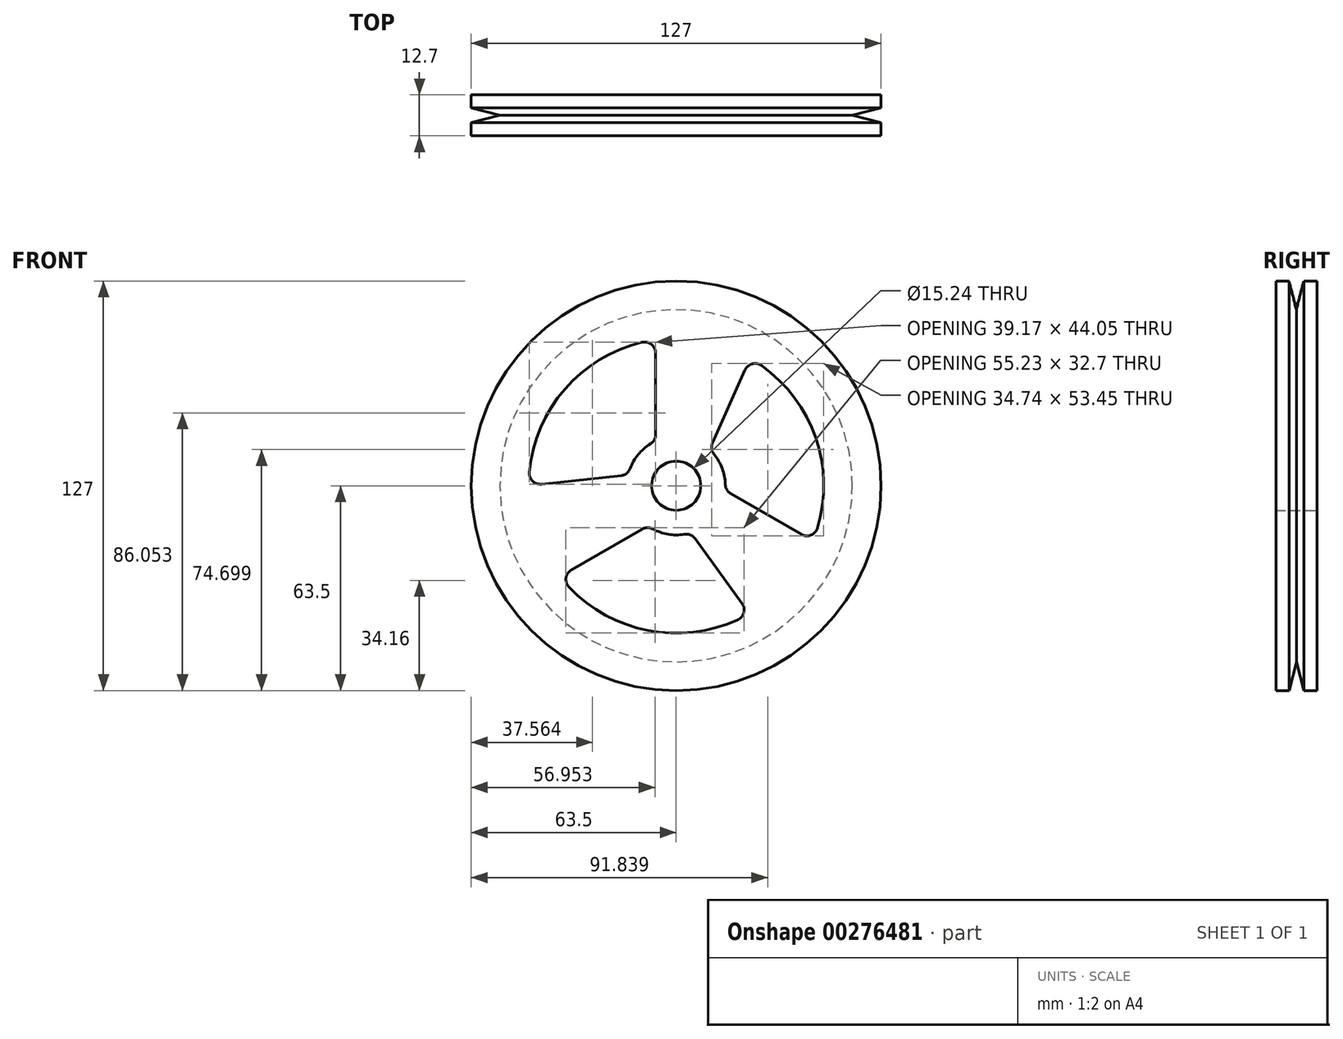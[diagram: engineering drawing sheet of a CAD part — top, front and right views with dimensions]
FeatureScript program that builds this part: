
annotation { "Feature Type Name" : "Feature", "Feature Type Description" : "" }
export const myFeature = defineFeature(function(context is Context, id is Id, definition is map)
    precondition{}
    {
        {
            var Q0;
            Q0=qCreatedBy(makeId("Front.planeOp"),FACE);
            var sketch = newSketch(context, id + "F0", { "sketchPlane" : qUnion([Q0])});
            skCircle(sketch, "E0", {"center": v(0, 0) * mm, "radius": 63.5 * mm});
            skArc(sketch, "E1.0", {"start": v(-10.56, 44.48) * mm, "mid": v(-34.51, 29.99) * mm, "end": v(-45.52, 4.25) * mm});
            skArc(sketch, "E2", {"start": v(-7.98, 12.98) * mm, "mid": v(-11.77, 9.68) * mm, "end": v(-14.28, 5.32) * mm});
            skCircle(sketch, "E3", {"center": v(0, 0) * mm, "radius": 7.62 * mm});
            skLineSegment(sketch, "E4.trimOffspring", {"start": v(-6.35, 41.15) * mm, "end": v(-6.35, 15.9) * mm});
            skLineSegment(sketch, "E5.trimOffspring", {"start": v(21.34, 35.9) * mm, "end": v(11.26, 13.28) * mm});
            skPoint(sketch, "E6.start.orphan", {"position": v(0, 46.5) * mm});
            skLineSegment(sketch, "E7.1.0", {"start": v(-32.46, -26.08) * mm, "end": v(-10.6, -13.45) * mm});
            skLineSegment(sketch, "E7.1.1", {"start": v(-41.76, 0.53) * mm, "end": v(-17.13, 3.12) * mm});
            skLineSegment(sketch, "E7.2.0", {"start": v(38.81, -15.08) * mm, "end": v(16.94, -2.45) * mm});
            skLineSegment(sketch, "E7.2.1", {"start": v(20.42, -36.43) * mm, "end": v(5.87, -16.4) * mm});
            skArc(sketch, "E8.trimOffspring", {"start": v(-33.24, -31.4) * mm, "mid": v(-8.72, -44.88) * mm, "end": v(19.08, -41.55) * mm});
            skArc(sketch, "E9.trimOffspring", {"start": v(-7.25, -13.4) * mm, "mid": v(-2.5, -15.03) * mm, "end": v(2.53, -15.03) * mm});
            skArc(sketch, "E10.trimOffspring", {"start": v(15.23, 0.42) * mm, "mid": v(14.27, 5.35) * mm, "end": v(11.75, 9.7) * mm});
            skArc(sketch, "E11.trimOffspring", {"start": v(43.8, -13.1) * mm, "mid": v(43.23, 14.9) * mm, "end": v(26.44, 37.3) * mm});
            skPoint(sketch, "E12.visualSharp", {"position": v(-6.35, 45.28) * mm});
            skArc(sketch, "E12.filletArc", {"start": v(-6.35, 41.15) * mm, "mid": v(-7.65, 43.84) * mm, "end": v(-10.56, 44.48) * mm});
            skPoint(sketch, "E13.visualSharp", {"position": v(-6.35, 13.85) * mm});
            skArc(sketch, "E13.filletArc", {"start": v(-7.98, 12.98) * mm, "mid": v(-6.79, 14.23) * mm, "end": v(-6.35, 15.9) * mm});
            skPoint(sketch, "E14.visualSharp", {"position": v(-14.87, 3.35) * mm});
            skArc(sketch, "E14.filletArc", {"start": v(-17.13, 3.12) * mm, "mid": v(-15.4, 3.81) * mm, "end": v(-14.28, 5.32) * mm});
            skPoint(sketch, "E15.visualSharp", {"position": v(-45.72, 0.11) * mm});
            skArc(sketch, "E15.filletArc", {"start": v(-45.52, 4.25) * mm, "mid": v(-44.52, 1.5) * mm, "end": v(-41.76, 0.53) * mm});
            skPoint(sketch, "E16.visualSharp", {"position": v(-8.82, -12.43) * mm});
            skArc(sketch, "E16.filletArc", {"start": v(-7.25, -13.4) * mm, "mid": v(-8.93, -13) * mm, "end": v(-10.6, -13.45) * mm});
            skPoint(sketch, "E17.visualSharp", {"position": v(-36.04, -28.14) * mm});
            skArc(sketch, "E17.filletArc", {"start": v(-33.7, -27.3) * mm, "mid": v(-33.95, -30.27) * mm, "end": v(-31.77, -32.3) * mm});
            skArc(sketch, "E18.filletArc", {"start": v(-32.46, -26.08) * mm, "mid": v(-34.14, -28.54) * mm, "end": v(-33.24, -31.4) * mm});
            skPoint(sketch, "E19.visualSharp", {"position": v(22.76, -39.65) * mm});
            skArc(sketch, "E19.filletArc", {"start": v(18.97, -41.6) * mm, "mid": v(20.95, -39.36) * mm, "end": v(20.42, -36.43) * mm});
            skArc(sketch, "E20.filletArc", {"start": v(19.08, -41.55) * mm, "mid": v(20.96, -39.3) * mm, "end": v(20.42, -36.43) * mm});
            skPoint(sketch, "E21.visualSharp", {"position": v(4.53, -14.55) * mm});
            skArc(sketch, "E21.filletArc", {"start": v(5.87, -16.4) * mm, "mid": v(4.4, -15.24) * mm, "end": v(2.53, -15.03) * mm});
            skPoint(sketch, "E22.visualSharp", {"position": v(15.17, -1.43) * mm});
            skArc(sketch, "E22.filletArc", {"start": v(15.23, 0.42) * mm, "mid": v(15.72, -1.24) * mm, "end": v(16.94, -2.45) * mm});
            skPoint(sketch, "E23.visualSharp", {"position": v(42.39, -17.14) * mm});
            skArc(sketch, "E23.filletArc", {"start": v(38.81, -15.08) * mm, "mid": v(41.8, -15.3) * mm, "end": v(43.8, -13.1) * mm});
            skPoint(sketch, "E24.visualSharp", {"position": v(10.34, 11.2) * mm});
            skArc(sketch, "E24.filletArc", {"start": v(11.26, 13.28) * mm, "mid": v(11, 11.42) * mm, "end": v(11.75, 9.7) * mm});
            skPoint(sketch, "E25.visualSharp", {"position": v(22.96, 39.54) * mm});
            skArc(sketch, "E25.filletArc", {"start": v(26.44, 37.3) * mm, "mid": v(23.56, 37.8) * mm, "end": v(21.34, 35.9) * mm});
            skSolve(sketch);
        }
        {
            var Q0;
            Q0=makeQuery(id+"F0.imprint","IMPRINT",FACE,{"disambiguationData":[TD([[makeQuery(id+"F0.imprint","IMPRINT",EDGE,{"derivedFrom":sQuery(id+"F0.wireOp",EDGE,"E0")}),1.0]])]});
            extrude(context, id + "F1", {"entities" : qUnion([Q0]), "endBound" : BoundingType.SYMMETRIC, "depth" : 12.7 * mm});
        }
        {
            var Q0;
            Q0=qCreatedBy(makeId("Right.planeOp"),FACE);
            var sketch = newSketch(context, id + "F2", { "sketchPlane" : qUnion([Q0])});
            skLineSegment(sketch, "E26", {"start": v(0, 54.6) * mm, "end": v(0, 63.5) * mm});
            skLineSegment(sketch, "E27", {"start": v(0, 63.5) * mm, "end": v(-2.29, 63.5) * mm});
            skLineSegment(sketch, "E28", {"start": v(-2.29, 63.5) * mm, "end": v(0, 54.6) * mm});
            skLineSegment(sketch, "E29.MirrorCS", {"start": v(0, 63.5) * mm, "end": v(2.29, 63.5) * mm});
            skLineSegment(sketch, "E30.MirrorCS", {"start": v(2.29, 63.5) * mm, "end": v(0, 54.6) * mm});
            skLineSegment(sketch, "E31", {"start": v(-48.66, 0) * mm, "end": v(40.07, 0) * mm, "construction": true});
            skSolve(sketch);
        }
        {
            var Q0;
            Q0 = qSketchRegion(id + "F2", true);
            var Q1;
            Q1=sQuery(id+"F2.wireOp",EDGE,"E31");
            revolve(context, id + "F3", {"operationType" : NewBodyOperationType.REMOVE, "entities" : qUnion([Q0]), "axis" : qUnion([Q1]), "revolveType" : RevolveType.FULL, "oppositeDirection" : true});
        }
    });
